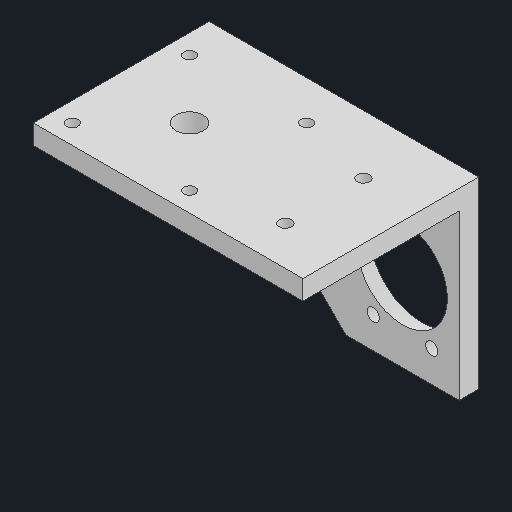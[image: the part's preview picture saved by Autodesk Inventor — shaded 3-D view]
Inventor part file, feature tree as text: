
AUTODESK INVENTOR PART (.ipt)
format: ipt  version: 2025.1 (Build 291241000, 241)  size: 120,832 bytes
history: native  units: mm
features: other x3, sketch x2
ambient origin geometry x8: Origin, YZ Plane, XZ Plane, XY Plane, X Axis, Y Axis, Z Axis, Center Point
bodies: Solid1 (feature_tree)
feature tree (5):
  other  "Tensioner Top.ipt"
  other  "Solid1::Tensioner Top.ipt"
  other  "TaggingFeature1"
  sketch  "Sketch1"  dims[d0=10.0mm]
  sketch  "Sketch2"
